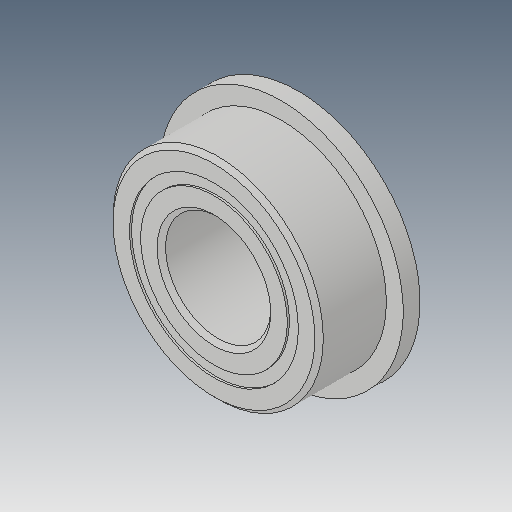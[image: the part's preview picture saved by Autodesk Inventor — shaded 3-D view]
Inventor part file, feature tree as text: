
AUTODESK INVENTOR PART (.ipt)
format: ipt  version: 2018 (Build 220112000, 112)  size: 613,888 bytes
history: native  units: in
note: dims shown in document units (in); Inventor stores cm internally (conversion verified against a paired STEP export)
features: other x11, revolve x5
ambient origin geometry x8: Origin, YZ Plane, XZ Plane, XY Plane, X Axis, Y Axis, Z Axis, Center Point
bodies: Solid1 (feature_tree), Solid2 (feature_tree), Solid3 (feature_tree), Solid4 (feature_tree), Solid5 (feature_tree), Solid6 (feature_tree), Solid7 (feature_tree), Solid8 (feature_tree), Solid9 (feature_tree), Solid10 (feature_tree), Solid11 (feature_tree), Solid12 (feature_tree), Solid13 (feature_tree), Solid14 (feature_tree), Solid15 (feature_tree), Solid16 (feature_tree)
feature tree (16):
  revolve  "Revolve3"  [1 undecoded]
  revolve  "Revolve4"  [1 undecoded]
  other  "CirPattern1[1]"
  other  "CirPattern1[2]"
  other  "CirPattern1[3]"
  other  "CirPattern1[4]"
  other  "CirPattern1[5]"
  other  "CirPattern1[6]"
  other  "CirPattern1[7]"
  other  "CirPattern1[8]"
  other  "CirPattern1[9]"
  other  "CirPattern1[10]"
  other  "CirPattern1[11]"
  revolve  "Revolve5[1]"  [1 undecoded]
  revolve  "Revolve5[2]"  [1 undecoded]
  revolve  "Revolve6"  [1 undecoded]
note: 5 required parameter values undecoded (feature->parameter linkage not recoverable at this tier; creation-order binding heuristic only, values carry confidence <= 0.55)
